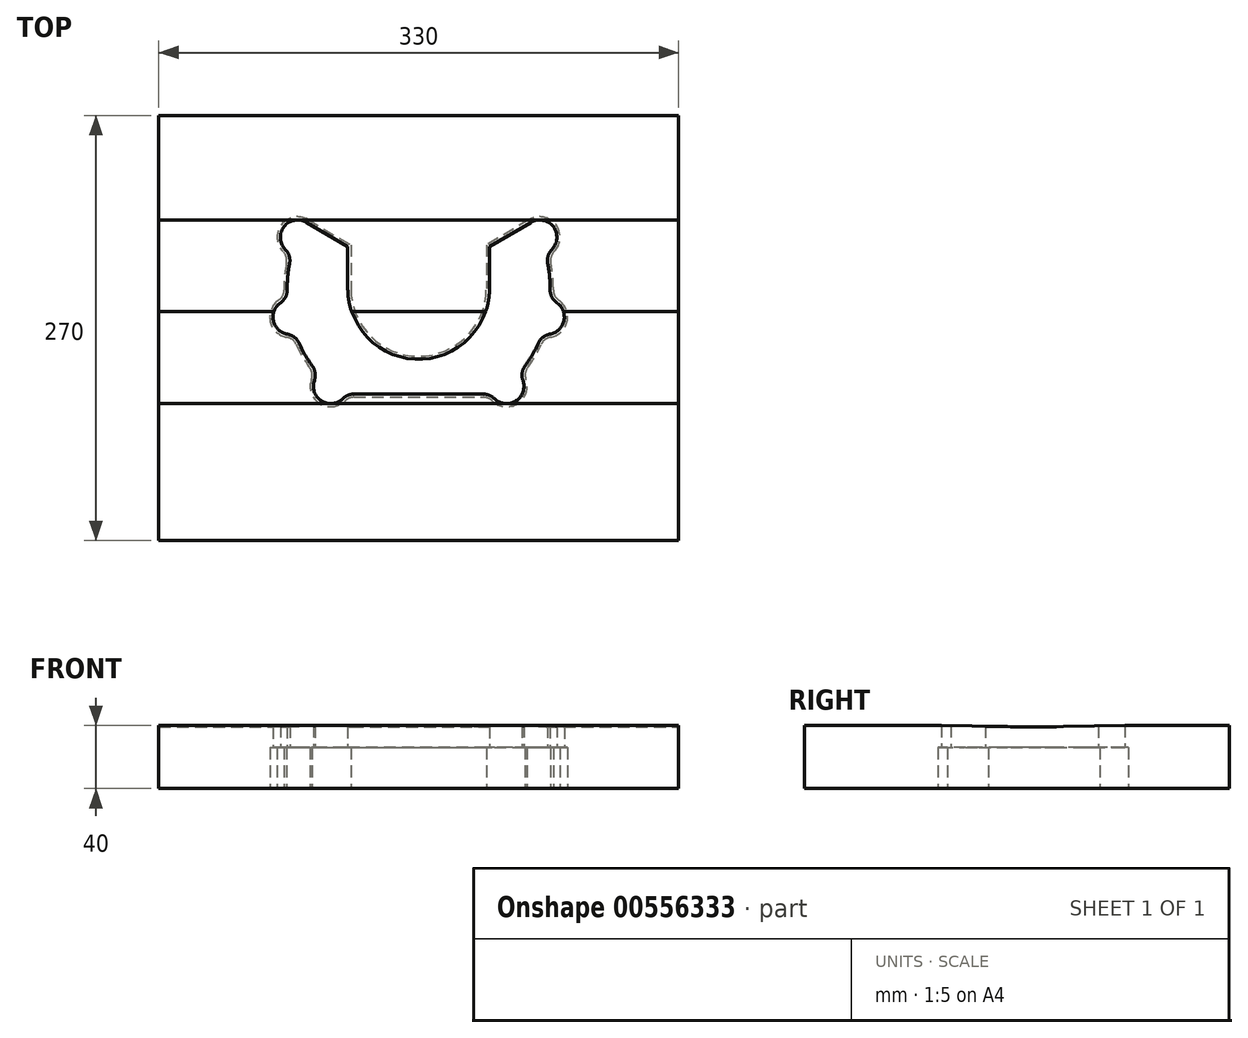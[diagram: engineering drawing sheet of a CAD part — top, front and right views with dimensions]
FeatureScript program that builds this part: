
annotation { "Feature Type Name" : "Feature", "Feature Type Description" : "" }
export const myFeature = defineFeature(function(context is Context, id is Id, definition is map)
    precondition{}
    {
        {
            var Q0;
            Q0=qCreatedBy(makeId("Top.planeOp"),FACE);
            var sketch = newSketch(context, id + "F0", { "sketchPlane" : qUnion([Q0])});
            skLineSegment(sketch, "E0.bottom", {"start": v(165, 135) * mm, "end": v(-165, 135) * mm});
            skLineSegment(sketch, "E0.top", {"start": v(165, -135) * mm, "end": v(-165, -135) * mm});
            skLineSegment(sketch, "E0.left", {"start": v(165, 135) * mm, "end": v(165, -135) * mm});
            skLineSegment(sketch, "E0.right", {"start": v(-165, 135) * mm, "end": v(-165, -135) * mm});
            skPoint(sketch, "E0.middle", {"position": v(0, 0) * mm});
            skArc(sketch, "E1", {"start": v(-81.96, 40.94) * mm, "mid": v(-83.15, 32.64) * mm, "end": v(-83.5, 24.27) * mm});
            skLineSegment(sketch, "E2", {"start": v(-45, 44.1) * mm, "end": v(-76.86, 57.63) * mm});
            skLineSegment(sketch, "E3", {"start": v(0, 25) * mm, "end": v(-81.52, 6.93) * mm});
            skLineSegment(sketch, "E4", {"start": v(0, 25) * mm, "end": v(-55.88, -37.05) * mm});
            skLineSegment(sketch, "E5", {"start": v(0, 25) * mm, "end": v(55.88, -37.05) * mm});
            skLineSegment(sketch, "E6", {"start": v(0, 25) * mm, "end": v(81.52, 6.93) * mm});
            skLineSegment(sketch, "E7", {"start": v(45, 44.1) * mm, "end": v(76.86, 57.63) * mm});
            skLineSegment(sketch, "E8", {"start": v(0, 25) * mm, "end": v(-83.5, 25) * mm});
            skArc(sketch, "E9", {"start": v(-71.26, 67.1) * mm, "mid": v(-85.54, 64.4) * mm, "end": v(-84.68, 49.89) * mm});
            skArc(sketch, "E10", {"start": v(-87.8, 15.97) * mm, "mid": v(-92.26, 4.55) * mm, "end": v(-83.39, -3.91) * mm});
            skArc(sketch, "E11", {"start": v(-66.23, -33.34) * mm, "mid": v(-61.8, -46.32) * mm, "end": v(-48.15, -44.88) * mm});
            skArc(sketch, "E12", {"start": v(48.15, -44.88) * mm, "mid": v(61.8, -46.32) * mm, "end": v(66.23, -33.34) * mm});
            skArc(sketch, "E13", {"start": v(83.39, -3.91) * mm, "mid": v(92.26, 4.55) * mm, "end": v(87.8, 15.97) * mm});
            skArc(sketch, "E14", {"start": v(84.68, 49.89) * mm, "mid": v(85.54, 64.4) * mm, "end": v(71.26, 67.1) * mm});
            skLineSegment(sketch, "E15", {"start": v(-41.13, -42) * mm, "end": v(41.13, -42) * mm});
            skArc(sketch, "E16", {"start": v(-45, 25) * mm, "mid": v(0, -20) * mm, "end": v(45, 25) * mm});
            skLineSegment(sketch, "E17", {"start": v(62.6, 51.58) * mm, "end": v(67.67, 51.58) * mm});
            skLineSegment(sketch, "E18", {"start": v(-71.26, 67.1) * mm, "end": v(-45, 51.58) * mm});
            skLineSegment(sketch, "E19", {"start": v(71.26, 67.1) * mm, "end": v(45, 51.58) * mm});
            skLineSegment(sketch, "E20", {"start": v(45, 51.58) * mm, "end": v(45, 25) * mm});
            skLineSegment(sketch, "E21", {"start": v(-45, 51.58) * mm, "end": v(-45, 25) * mm});
            skArc(sketch, "E22.trimOffspring", {"start": v(83.5, 24.27) * mm, "mid": v(83.15, 32.64) * mm, "end": v(81.96, 40.94) * mm});
            skArc(sketch, "E23.trimOffspring", {"start": v(67.55, -24.08) * mm, "mid": v(72.13, -17.06) * mm, "end": v(75.99, -9.62) * mm});
            skArc(sketch, "E24.trimOffspring", {"start": v(-75.99, -9.62) * mm, "mid": v(-72.13, -17.06) * mm, "end": v(-67.55, -24.08) * mm});
            skArc(sketch, "E25.trimOffspring", {"start": v(66.74, 53.33) * mm, "mid": v(67.16, 52.43) * mm, "end": v(67.67, 51.58) * mm});
            skPoint(sketch, "E26.visualSharp", {"position": v(-80.48, 47.24) * mm});
            skArc(sketch, "E26.filletArc", {"start": v(-81.96, 40.94) * mm, "mid": v(-82.2, 45.75) * mm, "end": v(-84.68, 49.89) * mm});
            skPoint(sketch, "E27.visualSharp", {"position": v(-83.19, 17.8) * mm});
            skArc(sketch, "E27.filletArc", {"start": v(-87.8, 15.97) * mm, "mid": v(-84.62, 19.58) * mm, "end": v(-83.5, 24.27) * mm});
            skPoint(sketch, "E28.visualSharp", {"position": v(-78.44, -3.63) * mm});
            skArc(sketch, "E28.filletArc", {"start": v(-75.99, -9.62) * mm, "mid": v(-78.98, -5.85) * mm, "end": v(-83.39, -3.91) * mm});
            skPoint(sketch, "E29.visualSharp", {"position": v(-63.55, -29.17) * mm});
            skArc(sketch, "E29.filletArc", {"start": v(-66.23, -33.34) * mm, "mid": v(-65.74, -28.54) * mm, "end": v(-67.55, -24.08) * mm});
            skPoint(sketch, "E30.visualSharp", {"position": v(-46.05, -42) * mm});
            skArc(sketch, "E30.filletArc", {"start": v(-41.13, -42) * mm, "mid": v(-44.92, -42.75) * mm, "end": v(-48.15, -44.88) * mm});
            skPoint(sketch, "E31.visualSharp", {"position": v(46.05, -42) * mm});
            skArc(sketch, "E31.filletArc", {"start": v(48.15, -44.88) * mm, "mid": v(44.92, -42.75) * mm, "end": v(41.13, -42) * mm});
            skPoint(sketch, "E32.visualSharp", {"position": v(63.55, -29.17) * mm});
            skArc(sketch, "E32.filletArc", {"start": v(67.55, -24.08) * mm, "mid": v(65.74, -28.54) * mm, "end": v(66.23, -33.34) * mm});
            skPoint(sketch, "E33.visualSharp", {"position": v(78.44, -3.63) * mm});
            skArc(sketch, "E33.filletArc", {"start": v(83.39, -3.91) * mm, "mid": v(78.98, -5.85) * mm, "end": v(75.99, -9.62) * mm});
            skPoint(sketch, "E34.visualSharp", {"position": v(83.19, 17.8) * mm});
            skArc(sketch, "E34.filletArc", {"start": v(83.5, 24.27) * mm, "mid": v(84.62, 19.58) * mm, "end": v(87.8, 15.97) * mm});
            skPoint(sketch, "E35.visualSharp", {"position": v(80.48, 47.24) * mm});
            skArc(sketch, "E35.filletArc", {"start": v(84.68, 49.89) * mm, "mid": v(82.2, 45.75) * mm, "end": v(81.96, 40.94) * mm});
            skLineSegment(sketch, "E36", {"start": v(-165, 25) * mm, "end": v(165, 25) * mm});
            skSolve(sketch);
        }
        {
            var Q0;
            {var subQ5=sQuery(id+"F0.wireOp",EDGE,"E0.top");Q0=makeQuery(id+"F0.imprint","IMPRINT",FACE,{"disambiguationData":[TD([[makeQuery(id+"F0.imprint","IMPRINT",EDGE,{"derivedFrom":subQ5}),-1.0]])]});}
            var Q1;
            {var subQ2=sQuery(id+"F0.wireOp",EDGE,"E0.bottom");Q1=makeQuery(id+"F0.imprint","IMPRINT",FACE,{"disambiguationData":[TD([[makeQuery(id+"F0.imprint","IMPRINT",EDGE,{"derivedFrom":subQ2}),1.0]])]});}
            var Q2;
            {var subQ1=sQuery(id+"F0.wireOp",EDGE,"E3");var subQ3=sQuery(id+"F0.wireOp",EDGE,"E16");var subQ4=makeQuery(id+"F0.imprint","INTERSECT",VERTEX,{"derivedFrom":[subQ1,subQ3]});Q2=makeQuery(id+"F0.imprint","IMPRINT",FACE,{"disambiguationData":[TD([[makeQuery(id+"F0.imprint","IMPRINT",EDGE,{"disambiguationData":[TD([[subQ4,1.0]])],"derivedFrom":subQ3}),1.0]])]});}
            var Q3;
            {var subQ1=sQuery(id+"F0.wireOp",EDGE,"E3");var subQ3=sQuery(id+"F0.wireOp",EDGE,"E16");var subQ4=makeQuery(id+"F0.imprint","INTERSECT",VERTEX,{"derivedFrom":[subQ1,subQ3]});Q3=makeQuery(id+"F0.imprint","IMPRINT",FACE,{"disambiguationData":[TD([[makeQuery(id+"F0.imprint","IMPRINT",EDGE,{"disambiguationData":[TD([[subQ4,-1.0]])],"derivedFrom":subQ3}),1.0]])]});}
            var Q4;
            {var subQ1=sQuery(id+"F0.wireOp",EDGE,"E4");var subQ3=sQuery(id+"F0.wireOp",EDGE,"E16");var subQ4=makeQuery(id+"F0.imprint","INTERSECT",VERTEX,{"derivedFrom":[subQ1,subQ3]});Q4=makeQuery(id+"F0.imprint","IMPRINT",FACE,{"disambiguationData":[TD([[makeQuery(id+"F0.imprint","IMPRINT",EDGE,{"disambiguationData":[TD([[subQ4,-1.0]])],"derivedFrom":subQ3}),1.0]])]});}
            var Q5;
            {var subQ1=sQuery(id+"F0.wireOp",EDGE,"E5");var subQ3=sQuery(id+"F0.wireOp",EDGE,"E16");var subQ4=makeQuery(id+"F0.imprint","INTERSECT",VERTEX,{"derivedFrom":[subQ1,subQ3]});Q5=makeQuery(id+"F0.imprint","IMPRINT",FACE,{"disambiguationData":[TD([[makeQuery(id+"F0.imprint","IMPRINT",EDGE,{"disambiguationData":[TD([[subQ4,-1.0]])],"derivedFrom":subQ3}),1.0]])]});}
            var Q6;
            {var subQ1=sQuery(id+"F0.wireOp",EDGE,"E6");var subQ3=sQuery(id+"F0.wireOp",EDGE,"E16");var subQ4=makeQuery(id+"F0.imprint","INTERSECT",VERTEX,{"derivedFrom":[subQ1,subQ3]});Q6=makeQuery(id+"F0.imprint","IMPRINT",FACE,{"disambiguationData":[TD([[makeQuery(id+"F0.imprint","IMPRINT",EDGE,{"disambiguationData":[TD([[subQ4,-1.0]])],"derivedFrom":subQ3}),1.0]])]});}
            extrude(context, id + "F1", {"entities" : qUnion([Q0, Q1, Q2, Q3, Q4, Q5, Q6]), "depth" : 40 * mm, "offsetDistance" : 25 * mm});
        }
        {
            var Q0;
            Q0=makeQuery(id+"F1.opExtrude","CAP_FACE",FACE,{"disambiguationData":[OSD([sQuery(id+"F0.wireOp",EDGE,"E0.bottom"),sQuery(id+"F0.wireOp",EDGE,"E0.top"),sQuery(id+"F0.wireOp",EDGE,"E0.left"),sQuery(id+"F0.wireOp",EDGE,"E0.right"),sQuery(id+"F0.wireOp",EDGE,"E1"),sQuery(id+"F0.wireOp",EDGE,"E9"),sQuery(id+"F0.wireOp",EDGE,"E10"),sQuery(id+"F0.wireOp",EDGE,"E11"),sQuery(id+"F0.wireOp",EDGE,"E12"),sQuery(id+"F0.wireOp",EDGE,"E13"),sQuery(id+"F0.wireOp",EDGE,"E14"),sQuery(id+"F0.wireOp",EDGE,"E15"),sQuery(id+"F0.wireOp",EDGE,"E16"),sQuery(id+"F0.wireOp",EDGE,"E18"),sQuery(id+"F0.wireOp",EDGE,"E19"),sQuery(id+"F0.wireOp",EDGE,"E20"),sQuery(id+"F0.wireOp",EDGE,"E21"),sQuery(id+"F0.wireOp",EDGE,"E22.trimOffspring"),sQuery(id+"F0.wireOp",EDGE,"E23.trimOffspring"),sQuery(id+"F0.wireOp",EDGE,"E24.trimOffspring"),sQuery(id+"F0.wireOp",EDGE,"E26.filletArc"),sQuery(id+"F0.wireOp",EDGE,"E27.filletArc"),sQuery(id+"F0.wireOp",EDGE,"E28.filletArc"),sQuery(id+"F0.wireOp",EDGE,"E29.filletArc"),sQuery(id+"F0.wireOp",EDGE,"E30.filletArc"),sQuery(id+"F0.wireOp",EDGE,"E31.filletArc"),sQuery(id+"F0.wireOp",EDGE,"E32.filletArc"),sQuery(id+"F0.wireOp",EDGE,"E33.filletArc"),sQuery(id+"F0.wireOp",EDGE,"E34.filletArc"),sQuery(id+"F0.wireOp",EDGE,"E35.filletArc")])],"isStart":true});
            var sketch = newSketch(context, id + "F2", { "sketchPlane" : qUnion([Q0])});
            skLineSegment(sketch, "E37.0", {"start": v(-71.26, -67.1) * mm, "end": v(-45, -51.58) * mm});
            skArc(sketch, "E38.0", {"start": v(-71.26, -67.1) * mm, "mid": v(-85.54, -64.4) * mm, "end": v(-84.68, -49.89) * mm});
            skArc(sketch, "E39.0", {"start": v(-81.96, -40.94) * mm, "mid": v(-82.2, -45.75) * mm, "end": v(-84.68, -49.89) * mm});
            skArc(sketch, "E40.0", {"start": v(-81.96, -40.94) * mm, "mid": v(-83.15, -32.64) * mm, "end": v(-83.5, -24.27) * mm});
            skArc(sketch, "E41.0", {"start": v(-87.8, -15.97) * mm, "mid": v(-84.62, -19.58) * mm, "end": v(-83.5, -24.27) * mm});
            skArc(sketch, "E42.0", {"start": v(-87.8, -15.97) * mm, "mid": v(-92.26, -4.55) * mm, "end": v(-83.39, 3.91) * mm});
            skArc(sketch, "E43.0", {"start": v(-75.99, 9.62) * mm, "mid": v(-78.98, 5.85) * mm, "end": v(-83.39, 3.91) * mm});
            skArc(sketch, "E44.0", {"start": v(-75.99, 9.62) * mm, "mid": v(-72.13, 17.06) * mm, "end": v(-67.55, 24.08) * mm});
            skArc(sketch, "E45.0", {"start": v(-66.23, 33.34) * mm, "mid": v(-65.74, 28.54) * mm, "end": v(-67.55, 24.08) * mm});
            skArc(sketch, "E46.0", {"start": v(-66.23, 33.34) * mm, "mid": v(-61.8, 46.32) * mm, "end": v(-48.15, 44.88) * mm});
            skLineSegment(sketch, "E47.0", {"start": v(-45, -51.58) * mm, "end": v(-45, -25) * mm});
            skArc(sketch, "E48.0", {"start": v(-45, -25) * mm, "mid": v(0, 20) * mm, "end": v(45, -25) * mm});
            skLineSegment(sketch, "E49.0", {"start": v(45, -51.58) * mm, "end": v(45, -25) * mm});
            skLineSegment(sketch, "E50.0", {"start": v(71.26, -67.1) * mm, "end": v(45, -51.58) * mm});
            skArc(sketch, "E51.0", {"start": v(84.68, -49.89) * mm, "mid": v(85.54, -64.4) * mm, "end": v(71.26, -67.1) * mm});
            skArc(sketch, "E52.0", {"start": v(84.68, -49.89) * mm, "mid": v(82.2, -45.75) * mm, "end": v(81.96, -40.94) * mm});
            skArc(sketch, "E53.0", {"start": v(83.5, -24.27) * mm, "mid": v(83.15, -32.64) * mm, "end": v(81.96, -40.94) * mm});
            skArc(sketch, "E54.0", {"start": v(83.5, -24.27) * mm, "mid": v(84.62, -19.58) * mm, "end": v(87.8, -15.97) * mm});
            skArc(sketch, "E55.0", {"start": v(83.39, 3.91) * mm, "mid": v(92.26, -4.55) * mm, "end": v(87.8, -15.97) * mm});
            skArc(sketch, "E56.0", {"start": v(83.39, 3.91) * mm, "mid": v(78.98, 5.85) * mm, "end": v(75.99, 9.62) * mm});
            skArc(sketch, "E57.0", {"start": v(67.55, 24.08) * mm, "mid": v(72.13, 17.06) * mm, "end": v(75.99, 9.62) * mm});
            skArc(sketch, "E58.0", {"start": v(67.55, 24.08) * mm, "mid": v(65.74, 28.54) * mm, "end": v(66.23, 33.34) * mm});
            skArc(sketch, "E59.0", {"start": v(48.15, 44.88) * mm, "mid": v(61.8, 46.32) * mm, "end": v(66.23, 33.34) * mm});
            skArc(sketch, "E60.0", {"start": v(48.15, 44.88) * mm, "mid": v(44.92, 42.75) * mm, "end": v(41.13, 42) * mm});
            skLineSegment(sketch, "E61.0", {"start": v(-41.13, 42) * mm, "end": v(41.13, 42) * mm});
            skArc(sketch, "E62.0", {"start": v(-41.13, 42) * mm, "mid": v(-44.92, 42.75) * mm, "end": v(-48.15, 44.88) * mm});
            skArc(sketch, "E63.0", {"start": v(-41.13, 44) * mm, "mid": v(-44.16, 44.6) * mm, "end": v(-46.75, 46.3) * mm});
            skArc(sketch, "E63.1", {"start": v(-68.11, 32.66) * mm, "mid": v(-62.87, 48) * mm, "end": v(-46.75, 46.3) * mm});
            skArc(sketch, "E63.2", {"start": v(-68.11, 32.66) * mm, "mid": v(-67.72, 28.83) * mm, "end": v(-69.17, 25.26) * mm});
            skArc(sketch, "E63.3", {"start": v(86.1, -48.48) * mm, "mid": v(87.11, -65.62) * mm, "end": v(70.25, -68.82) * mm});
            skArc(sketch, "E63.4", {"start": v(86.1, -48.48) * mm, "mid": v(84.12, -45.17) * mm, "end": v(83.93, -41.32) * mm});
            skArc(sketch, "E63.5", {"start": v(85.5, -24.25) * mm, "mid": v(85.14, -32.83) * mm, "end": v(83.93, -41.32) * mm});
            skArc(sketch, "E63.6", {"start": v(85.5, -24.25) * mm, "mid": v(86.4, -20.5) * mm, "end": v(88.93, -17.6) * mm});
            skArc(sketch, "E63.7", {"start": v(83.73, 5.88) * mm, "mid": v(94.21, -4.12) * mm, "end": v(88.93, -17.6) * mm});
            skArc(sketch, "E63.8", {"start": v(83.73, 5.88) * mm, "mid": v(80.2, 7.43) * mm, "end": v(77.8, 10.45) * mm});
            skArc(sketch, "E63.9", {"start": v(46.75, 46.3) * mm, "mid": v(44.16, 44.6) * mm, "end": v(41.13, 44) * mm});
            skArc(sketch, "E63.10", {"start": v(46.75, 46.3) * mm, "mid": v(62.87, 48) * mm, "end": v(68.11, 32.66) * mm});
            skArc(sketch, "E63.11", {"start": v(69.17, 25.26) * mm, "mid": v(67.72, 28.83) * mm, "end": v(68.11, 32.66) * mm});
            skArc(sketch, "E63.12", {"start": v(69.17, 25.26) * mm, "mid": v(73.86, 18.07) * mm, "end": v(77.8, 10.45) * mm});
            skLineSegment(sketch, "E63.13", {"start": v(70.25, -68.82) * mm, "end": v(43, -52.72) * mm});
            skLineSegment(sketch, "E63.14", {"start": v(43, -52.72) * mm, "end": v(43, -25) * mm});
            skArc(sketch, "E63.15", {"start": v(-43, -25) * mm, "mid": v(0, 18) * mm, "end": v(43, -25) * mm});
            skLineSegment(sketch, "E63.16", {"start": v(-41.13, 44) * mm, "end": v(41.13, 44) * mm});
            skLineSegment(sketch, "E63.17", {"start": v(-43, -52.72) * mm, "end": v(-43, -25) * mm});
            skLineSegment(sketch, "E63.18", {"start": v(-70.25, -68.82) * mm, "end": v(-43, -52.72) * mm});
            skArc(sketch, "E63.19", {"start": v(-70.25, -68.82) * mm, "mid": v(-87.11, -65.62) * mm, "end": v(-86.1, -48.48) * mm});
            skArc(sketch, "E63.20", {"start": v(-83.93, -41.32) * mm, "mid": v(-84.12, -45.17) * mm, "end": v(-86.1, -48.48) * mm});
            skArc(sketch, "E63.21", {"start": v(-83.93, -41.32) * mm, "mid": v(-85.14, -32.83) * mm, "end": v(-85.5, -24.25) * mm});
            skArc(sketch, "E63.22", {"start": v(-88.93, -17.6) * mm, "mid": v(-86.4, -20.5) * mm, "end": v(-85.5, -24.25) * mm});
            skArc(sketch, "E63.23", {"start": v(-88.93, -17.6) * mm, "mid": v(-94.21, -4.12) * mm, "end": v(-83.73, 5.88) * mm});
            skArc(sketch, "E63.24", {"start": v(-77.8, 10.45) * mm, "mid": v(-80.2, 7.43) * mm, "end": v(-83.73, 5.88) * mm});
            skArc(sketch, "E63.25", {"start": v(-77.8, 10.45) * mm, "mid": v(-73.86, 18.07) * mm, "end": v(-69.17, 25.26) * mm});
            skSolve(sketch);
        }
        {
            var Q0;
            Q0 = qSketchRegion(id + "F2", true);
            extrude(context, id + "F3", {"entities" : qUnion([Q0]), "operationType" : NewBodyOperationType.REMOVE, "oppositeDirection" : true, "depth" : 26 * mm, "offsetDistance" : 25 * mm});
        }
        {
            var Q0;
            Q0=makeQuery(id+"F1.opExtrude","CAP_FACE",FACE,{"disambiguationData":[OSD([sQuery(id+"F0.wireOp",EDGE,"E0.bottom"),sQuery(id+"F0.wireOp",EDGE,"E0.top"),sQuery(id+"F0.wireOp",EDGE,"E0.left"),sQuery(id+"F0.wireOp",EDGE,"E0.right"),sQuery(id+"F0.wireOp",EDGE,"E1"),sQuery(id+"F0.wireOp",EDGE,"E9"),sQuery(id+"F0.wireOp",EDGE,"E10"),sQuery(id+"F0.wireOp",EDGE,"E11"),sQuery(id+"F0.wireOp",EDGE,"E12"),sQuery(id+"F0.wireOp",EDGE,"E13"),sQuery(id+"F0.wireOp",EDGE,"E14"),sQuery(id+"F0.wireOp",EDGE,"E15"),sQuery(id+"F0.wireOp",EDGE,"E16"),sQuery(id+"F0.wireOp",EDGE,"E18"),sQuery(id+"F0.wireOp",EDGE,"E19"),sQuery(id+"F0.wireOp",EDGE,"E20"),sQuery(id+"F0.wireOp",EDGE,"E21"),sQuery(id+"F0.wireOp",EDGE,"E22.trimOffspring"),sQuery(id+"F0.wireOp",EDGE,"E23.trimOffspring"),sQuery(id+"F0.wireOp",EDGE,"E24.trimOffspring"),sQuery(id+"F0.wireOp",EDGE,"E26.filletArc"),sQuery(id+"F0.wireOp",EDGE,"E27.filletArc"),sQuery(id+"F0.wireOp",EDGE,"E28.filletArc"),sQuery(id+"F0.wireOp",EDGE,"E29.filletArc"),sQuery(id+"F0.wireOp",EDGE,"E30.filletArc"),sQuery(id+"F0.wireOp",EDGE,"E31.filletArc"),sQuery(id+"F0.wireOp",EDGE,"E32.filletArc"),sQuery(id+"F0.wireOp",EDGE,"E33.filletArc"),sQuery(id+"F0.wireOp",EDGE,"E34.filletArc"),sQuery(id+"F0.wireOp",EDGE,"E35.filletArc")])],"isStart":false});
            var sketch = newSketch(context, id + "F4", { "sketchPlane" : qUnion([Q0])});
            skLineSegment(sketch, "E64", {"start": v(76.86, 68.63) * mm, "end": v(165, 68.63) * mm});
            skLineSegment(sketch, "E65", {"start": v(55.88, -48.05) * mm, "end": v(165, -48.05) * mm});
            skLineSegment(sketch, "E66", {"start": v(165, -48.05) * mm, "end": v(165, 68.63) * mm});
            skSolve(sketch);
        }
        {
            var Q0;
            Q0=makeQuery(id+"F1.opExtrude","SWEPT_FACE",FACE,{"disambiguationData":[OSD([sQuery(id+"F0.wireOp",EDGE,"E0.left")])]});
            var sketch = newSketch(context, id + "F5", { "sketchPlane" : qUnion([Q0])});
            skLineSegment(sketch, "E67.0", {"start": v(-48.05, 40) * mm, "end": v(68.63, 40) * mm});
            skLineSegment(sketch, "E68", {"start": v(10.3, 40) * mm, "end": v(10.3, 39) * mm});
            skLineSegment(sketch, "E69", {"start": v(-48.05, 40) * mm, "end": v(10.3, 39) * mm});
            skLineSegment(sketch, "E70", {"start": v(68.63, 40) * mm, "end": v(10.3, 39) * mm});
            skSolve(sketch);
        }
        {
            var Q0;
            {var subQ2=sQuery(id+"F5.wireOp",EDGE,"E68");Q0=makeQuery(id+"F5.imprint","IMPRINT",FACE,{"disambiguationData":[TD([[makeQuery(id+"F5.imprint","IMPRINT",EDGE,{"derivedFrom":subQ2}),-1.0]])]});}
            var Q1;
            {var subQ2=sQuery(id+"F5.wireOp",EDGE,"E68");Q1=makeQuery(id+"F5.imprint","IMPRINT",FACE,{"disambiguationData":[TD([[makeQuery(id+"F5.imprint","IMPRINT",EDGE,{"derivedFrom":subQ2}),1.0]])]});}
            extrude(context, id + "F6", {"entities" : qUnion([Q0, Q1]), "operationType" : NewBodyOperationType.REMOVE, "oppositeDirection" : true, "depth" : 376 * mm, "offsetDistance" : 25 * mm});
        }
    });
